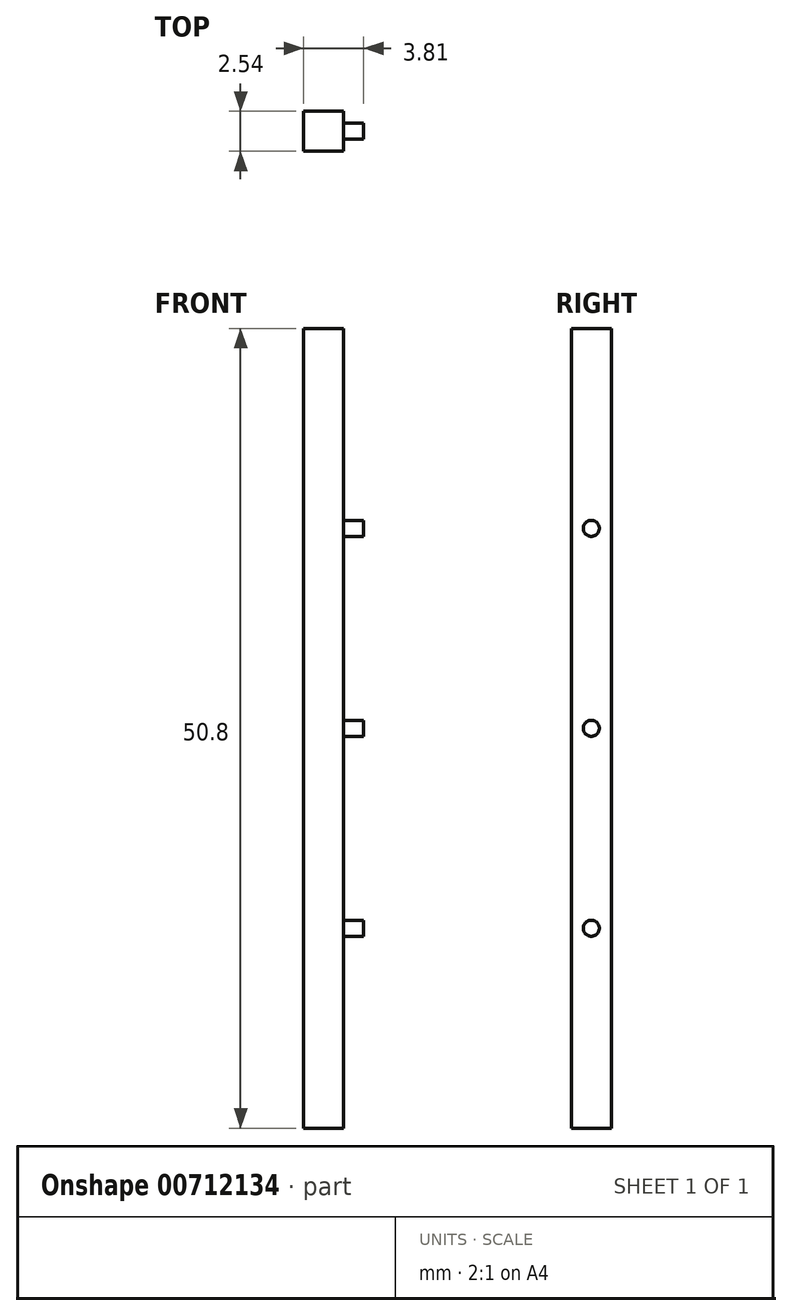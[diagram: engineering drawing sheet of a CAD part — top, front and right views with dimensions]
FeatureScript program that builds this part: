
annotation { "Feature Type Name" : "Feature", "Feature Type Description" : "" }
export const myFeature = defineFeature(function(context is Context, id is Id, definition is map)
    precondition{}
    {
        {
            var Q0;
            Q0=qCreatedBy(makeId("Front.planeOp"),FACE);
            var sketch = newSketch(context, id + "F0", { "sketchPlane" : qUnion([Q0])});
            skLineSegment(sketch, "E0.bottom", {"start": v(-31.96, -21.58) * mm, "end": v(-34.5, -21.58) * mm});
            skLineSegment(sketch, "E0.top", {"start": v(-31.96, 29.22) * mm, "end": v(-34.5, 29.22) * mm});
            skLineSegment(sketch, "E0.left", {"start": v(-31.96, -21.58) * mm, "end": v(-31.96, 29.22) * mm});
            skLineSegment(sketch, "E0.right", {"start": v(-34.5, -21.58) * mm, "end": v(-34.5, 29.22) * mm});
            skPoint(sketch, "E0.middle", {"position": v(-33.23, 3.82) * mm});
            skSolve(sketch);
        }
        {
            var Q0;
            Q0=makeQuery(id+"F0.imprint","IMPRINT",FACE,{"disambiguationData":[TD([[makeQuery(id+"F0.imprint","IMPRINT",EDGE,{"derivedFrom":sQuery(id+"F0.wireOp",EDGE,"E0.bottom")}),-1.0]])]});
            extrude(context, id + "F1", {"entities" : qUnion([Q0]), "depth" : 2.54 * mm, "offsetDistance" : 25.4 * mm});
        }
        {
            var Q0;
            Q0=makeQuery(id+"F1.opExtrude","SWEPT_FACE",FACE,{"disambiguationData":[OSD([sQuery(id+"F0.wireOp",EDGE,"E0.left")])]});
            var sketch = newSketch(context, id + "F2", { "sketchPlane" : qUnion([Q0])});
            skCircle(sketch, "E1", {"center": v(-1.27, 16.52) * mm, "radius": 0.5 * mm});
            skCircle(sketch, "E2", {"center": v(-1.27, 3.82) * mm, "radius": 0.5 * mm});
            skCircle(sketch, "E3", {"center": v(-1.27, -8.88) * mm, "radius": 0.5 * mm});
            skSolve(sketch);
        }
        {
            var Q0;
            Q0=makeQuery(id+"F2.imprint","IMPRINT",FACE,{"disambiguationData":[TD([[makeQuery(id+"F2.imprint","IMPRINT",EDGE,{"derivedFrom":sQuery(id+"F2.wireOp",EDGE,"E1")}),1.0]])]});
            var Q1;
            Q1=makeQuery(id+"F2.imprint","IMPRINT",FACE,{"disambiguationData":[TD([[makeQuery(id+"F2.imprint","IMPRINT",EDGE,{"derivedFrom":sQuery(id+"F2.wireOp",EDGE,"E2")}),1.0]])]});
            extrude(context, id + "F3", {"entities" : qUnion([Q0, Q1]), "operationType" : NewBodyOperationType.ADD, "depth" : 1.27 * mm, "offsetDistance" : 25.4 * mm});
        }
        {
            var Q0;
            Q0=makeQuery(id+"F2.imprint","IMPRINT",FACE,{"disambiguationData":[TD([[makeQuery(id+"F2.imprint","IMPRINT",EDGE,{"derivedFrom":sQuery(id+"F2.wireOp",EDGE,"E3")}),1.0]])]});
            extrude(context, id + "F4", {"entities" : qUnion([Q0]), "operationType" : NewBodyOperationType.ADD, "depth" : 1.27 * mm, "offsetDistance" : 25.4 * mm});
        }
    });
